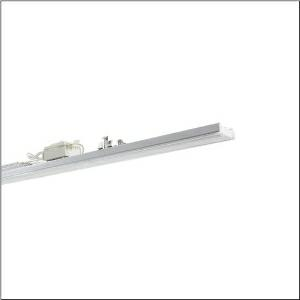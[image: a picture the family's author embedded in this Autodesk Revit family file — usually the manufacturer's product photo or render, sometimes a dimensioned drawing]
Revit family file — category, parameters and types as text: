
# Revit family: licross_r__21_recessed_mo_52te12dv4fxg3c_16ce
name_source: partatom
category: Lighting Fixtures
units: mm (PartAtom-declared; Revit-internal decimal feet)

## family parameters
Cut with Voids When Loaded = No
Host = Face
Light Source = No
Part Type = Normal
Room Calculation Point = No
Round Connector Dimension = Use Diameter
Shared = No

## types (1)
- --- (1 x LED, 950 lm, 5.5 W, 4000K)
    Apparent Load = 6 VA
    CIE Flux Codes = 72 92 99 100 100
    Color Rendering = 80
    Color Temperature = 4000K
    Default Elevation = 1800 mm
    Description = Licross® 21 Recessed MO, luminaire insert, of sheet steel, galvanised, coil coated, white, length: 2.250mm, width: 66mm, height: 67mm, LED rated luminous flux: 15.420lm, light colour: 840, control gear: DALI 2 (for two DALI lines), with plug, 6-pole, with phase selection, for trunking rail, 14-core, mains connection: 220..240V, AC, 50/60Hz, rated input power: 89W, for trunking rail, 14-core, internal wiring halogen-free, for emergency light function, converter,control gear: single battery element, battery: LiFePO4, 9Ah, primary optical cover: cover, of PMMA, light emission: direct distribution, primary light characteristic: symmetric, protection rating (complete): IP54, insulation class (complete): insulation class I (protective earthing), certification: CE, UKCA, protection symbol: D if used in an environment with non-conductive dust loads with corresponding accessories, impact resistance: IK06, permissible ambient temperature for indoor applications: +5..+35°C, standard: EN 60598-2-22, LABS conformity tested according to VDMA 24364:2018-05, reducing of maximum allowable ambient temperature of 5°C with ceiling mounting, corresponds to IFS (International Featured Standards) requirements for safety and quality in the food industry, packaging unit: 1 piece
    Height = 58 mm
    Lamp = 1 x LED
    Lamp Light Flux = 950 lm
    Lamp Power = 5.5 W
    Lamp count = 1
    Length = 2250 mm
    Luminous efficacy = 173 lm/W
    Manufacturer = Siteco
    ModVariant = No
    Model = 52TE12DV4FXG3C
    Mounting Place = Ceiling
    Mounting Type = Pendant
    Number of Poles = 1
    OnlyDefault = Yes
    Power Factor = 1
    Product Name = Licross® 21 Recessed MO
    Product group = luminaire insert | ceiling pendant
    ProductGroupID = 902
    Protection Class = Protection class I
    Protection Degree = IP 54
    RLX_Detail_Level = 1
    RLX_Emergency_Light_Flux = 0 lm
    RLX_Emergency_Type = 0
    RLX_Emergency_Type_DB = No
    RlxData = <blob elided: 29981 chars, md5=af319ff6>
    Socket = socket
    Standby Power = 0 W
    System Light Flux = 950 lm
    System Power = 6 W
    Type Comments = : emergency light operation: 3 h
    Type Image = l_1296930.jpg
    URL = http://relux.com
    VarID = @adj_131543
    Voltage = 0 V
    Weight = 0.00 kg
    Width = 66 mm

## geometry (parser evidence)
native form markers: Blend x4, Sweep x9
no freeform markers — native parametric forms only
